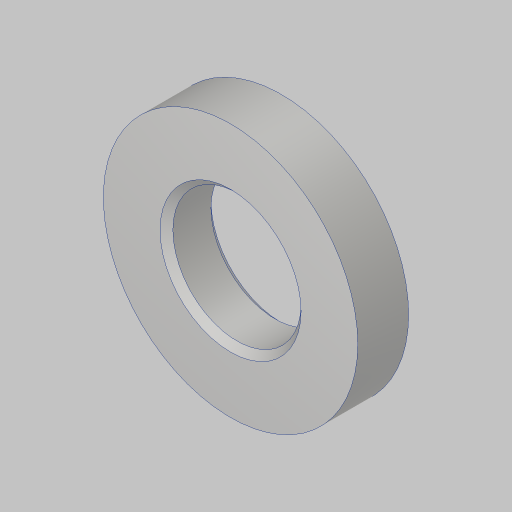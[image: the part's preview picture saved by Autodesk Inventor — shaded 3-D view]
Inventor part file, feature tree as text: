
AUTODESK INVENTOR PART (.ipt)
format: ipt  version: 2023.5 (Build 275446000, 446)  size: 112,128 bytes
history: native  units: in
note: dims shown in document units (in); Inventor stores cm internally (conversion verified against a paired STEP export)
features: extrude x1, chamfer x1, sketch x1
ambient origin geometry x8: Origin, YZ Plane, XZ Plane, XY Plane, X Axis, Y Axis, Z Axis, Center Point
bodies: Solid1 (feature_tree)
feature tree (3):
  extrude  "Extrusion1"  Depth=0.125in
  chamfer  "Chamfer1"  Distance=0.125in
  sketch  "Sketch1"  dims[d0=0.315in d2=0.625in d3=0.125in d4=0.0in d5=0.0157in d6=0.125in d7=45.0deg]
